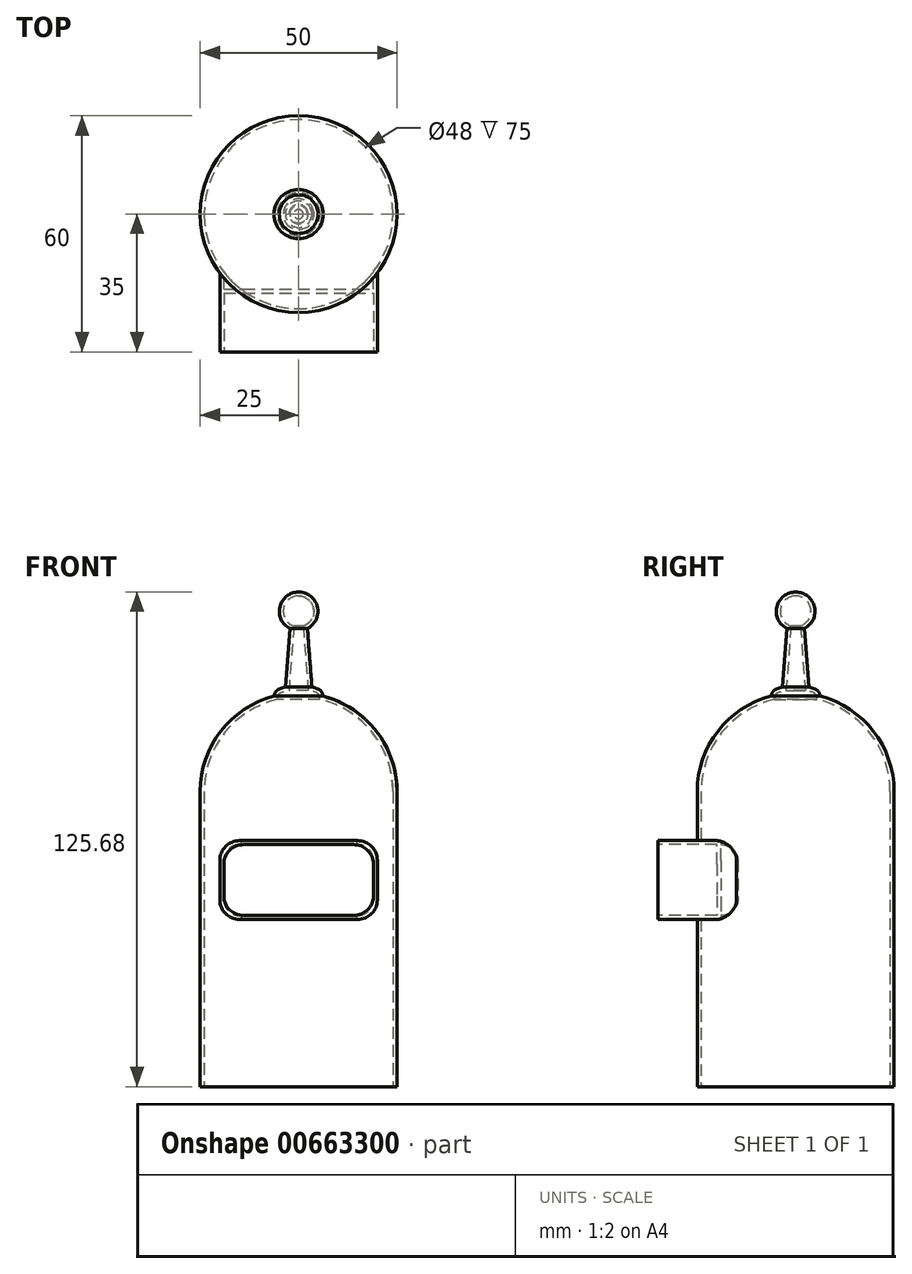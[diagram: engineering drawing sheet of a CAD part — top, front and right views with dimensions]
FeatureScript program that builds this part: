
annotation { "Feature Type Name" : "Feature", "Feature Type Description" : "" }
export const myFeature = defineFeature(function(context is Context, id is Id, definition is map)
    precondition{}
    {
        {
            var Q0;
            Q0=qCreatedBy(makeId("Top.planeOp"),FACE);
            var sketch = newSketch(context, id + "F0", { "sketchPlane" : qUnion([Q0])});
            skCircle(sketch, "E0", {"center": v(0, 0) * mm, "radius": 25 * mm});
            skSolve(sketch);
        }
        {
            var Q0;
            Q0=makeQuery(id+"F0.imprint","IMPRINT",FACE,{"disambiguationData":[TD([[makeQuery(id+"F0.imprint","IMPRINT",EDGE,{"derivedFrom":sQuery(id+"F0.wireOp",EDGE,"E0")}),1.0]])]});
            extrude(context, id + "F1", {"entities" : qUnion([Q0]), "endBound" : BoundingType.SYMMETRIC, "depth" : 75 * mm, "offsetDistance" : 25 * mm});
        }
        {
            var Q0;
            Q0=makeQuery(id+"F1.opExtrude","CAP_EDGE",EDGE,{"disambiguationData":[OSD([sQuery(id+"F0.wireOp",EDGE,"E0")])],"isStart":false});
            fillet(context, id + "F2", {"entities" : qUnion([Q0]), "radius" : 25 * mm, "tangentPropagation" : true, "allowEdgeOverflow" : false});
        }
        {
            var Q0;
            Q0=qCreatedBy(makeId("Front.planeOp"),FACE);
            var sketch = newSketch(context, id + "F3", { "sketchPlane" : qUnion([Q0])});
            skFitSpline(sketch, "E1", {"points": [v(-6.3, 36.49) * mm, v(-5.36, 38.3) * mm, v(-1.59, 39.32) * mm, v(0, 39.5) * mm], "startDerivative": vector(1.54, 6.57) * mm, "endDerivative": vector(4.86, 0.46) * mm});
            skLineSegment(sketch, "E2", {"start": v(-6.3, 36.49) * mm, "end": v(0, 36.49) * mm});
            skLineSegment(sketch, "E3", {"start": v(0, 36.49) * mm, "end": v(0, 39.5) * mm});
            skSolve(sketch);
        }
        {
            var Q0;
            Q0=qCreatedBy(makeId("Front.planeOp"),FACE);
            var sketch = newSketch(context, id + "F4", { "sketchPlane" : qUnion([Q0])});
            skLineSegment(sketch, "E4", {"start": v(0, 58.44) * mm, "end": v(0, 0) * mm, "construction": true});
            skSolve(sketch);
        }
        {
            var Q0;
            Q0=makeQuery(id+"F3.imprint","IMPRINT",FACE,{"disambiguationData":[TD([[makeQuery(id+"F3.imprint","IMPRINT",EDGE,{"derivedFrom":sQuery(id+"F3.wireOp",EDGE,"E1")}),-1.0]])]});
            var Q1;
            Q1=sQuery(id+"F4.wireOp",EDGE,"E4");
            revolve(context, id + "F5", {"operationType" : NewBodyOperationType.ADD, "entities" : qUnion([Q0]), "axis" : qUnion([Q1]), "revolveType" : RevolveType.FULL});
        }
        {
            var Q0;
            Q0=qCreatedBy(makeId("Front.planeOp"),FACE);
            var sketch = newSketch(context, id + "F6", { "sketchPlane" : qUnion([Q0])});
            skLineSegment(sketch, "E5", {"start": v(-3.38, 39.05) * mm, "end": v(-2.1, 55.68) * mm});
            skLineSegment(sketch, "E6", {"start": v(-2.1, 55.68) * mm, "end": v(0, 55.68) * mm});
            skLineSegment(sketch, "E7", {"start": v(0, 55.68) * mm, "end": v(0, 39.05) * mm});
            skLineSegment(sketch, "E8", {"start": v(-3.38, 39.05) * mm, "end": v(-3.38, 38.96) * mm});
            skLineSegment(sketch, "E9", {"start": v(-3.38, 38.96) * mm, "end": v(0, 38.96) * mm});
            skLineSegment(sketch, "E10", {"start": v(0, 38.96) * mm, "end": v(0, 39.05) * mm});
            skSolve(sketch);
        }
        {
            var Q0;
            Q0=makeQuery(id+"F6.imprint","IMPRINT",FACE,{"disambiguationData":[TD([[makeQuery(id+"F6.imprint","IMPRINT",EDGE,{"derivedFrom":sQuery(id+"F6.wireOp",EDGE,"E5")}),-1.0]])]});
            var Q1;
            Q1=sQuery(id+"F6.wireOp",EDGE,"E7");
            revolve(context, id + "F7", {"operationType" : NewBodyOperationType.ADD, "entities" : qUnion([Q0]), "axis" : qUnion([Q1]), "revolveType" : RevolveType.FULL});
        }
        {
            var Q0;
            Q0=qCreatedBy(makeId("Front.planeOp"),FACE);
            var sketch = newSketch(context, id + "F8", { "sketchPlane" : qUnion([Q0])});
            skArc(sketch, "E11", {"start": v(0, 63.18) * mm, "mid": v(-4.9, 58.28) * mm, "end": v(0, 53.38) * mm});
            skLineSegment(sketch, "E12", {"start": v(0, 53.38) * mm, "end": v(0, 63.18) * mm});
            skSolve(sketch);
        }
        {
            var Q0;
            Q0=makeQuery(id+"F8.imprint","IMPRINT",FACE,{"disambiguationData":[TD([[makeQuery(id+"F8.imprint","IMPRINT",EDGE,{"derivedFrom":sQuery(id+"F8.wireOp",EDGE,"E11")}),1.0]])]});
            var Q1;
            Q1=sQuery(id+"F8.wireOp",EDGE,"E12");
            revolve(context, id + "F9", {"operationType" : NewBodyOperationType.ADD, "entities" : qUnion([Q0]), "axis" : qUnion([Q1]), "revolveType" : RevolveType.FULL});
        }
        {
            var Q0;
            Q0=makeQuery(id+"F1.opExtrude","CAP_FACE",FACE,{"disambiguationData":[OSD([sQuery(id+"F0.wireOp",EDGE,"E0")])],"isStart":true});
            extrude(context, id + "F10", {"entities" : qUnion([Q0]), "operationType" : NewBodyOperationType.ADD, "depth" : 25 * mm, "offsetDistance" : 25 * mm});
        }
        {
            var Q0;
            Q0=qCreatedBy(makeId("Front.planeOp"),FACE);
            var sketch = newSketch(context, id + "F11", { "sketchPlane" : qUnion([Q0])});
            skLineSegment(sketch, "E13", {"start": v(0, 0) * mm, "end": v(-15, 0) * mm});
            skLineSegment(sketch, "E14", {"start": v(-20, -5) * mm, "end": v(-20, -15) * mm});
            skLineSegment(sketch, "E15", {"start": v(-15, -20) * mm, "end": v(15, -20) * mm});
            skLineSegment(sketch, "E16", {"start": v(20, -15) * mm, "end": v(20, -5) * mm});
            skLineSegment(sketch, "E17", {"start": v(15, 0) * mm, "end": v(0, 0) * mm});
            skPoint(sketch, "E18.visualSharp", {"position": v(-20, 0) * mm});
            skArc(sketch, "E18.filletArc", {"start": v(-15, 0) * mm, "mid": v(-18.54, -1.46) * mm, "end": v(-20, -5) * mm});
            skPoint(sketch, "E19.visualSharp", {"position": v(-20, -20) * mm});
            skArc(sketch, "E19.filletArc", {"start": v(-20, -15) * mm, "mid": v(-18.54, -18.54) * mm, "end": v(-15, -20) * mm});
            skPoint(sketch, "E20.visualSharp", {"position": v(20, -20) * mm});
            skArc(sketch, "E20.filletArc", {"start": v(15, -20) * mm, "mid": v(18.54, -18.54) * mm, "end": v(20, -15) * mm});
            skPoint(sketch, "E21.visualSharp", {"position": v(20, 0) * mm});
            skArc(sketch, "E21.filletArc", {"start": v(20, -5) * mm, "mid": v(18.54, -1.46) * mm, "end": v(15, 0) * mm});
            skSolve(sketch);
        }
        {
            var Q0;
            Q0 = qSketchRegion(id + "F11", true);
            extrude(context, id + "F12", {"entities" : qUnion([Q0]), "operationType" : NewBodyOperationType.ADD, "depth" : 35 * mm, "offsetDistance" : 25 * mm});
        }
        {
            var Q0;
            Q0=makeQuery(id+"F12.opExtrude","CAP_FACE",FACE,{"disambiguationData":[OSD([sQuery(id+"F11.wireOp",EDGE,"E13"),sQuery(id+"F11.wireOp",EDGE,"E14"),sQuery(id+"F11.wireOp",EDGE,"E15"),sQuery(id+"F11.wireOp",EDGE,"E16"),sQuery(id+"F11.wireOp",EDGE,"E17"),sQuery(id+"F11.wireOp",EDGE,"E18.filletArc"),sQuery(id+"F11.wireOp",EDGE,"E19.filletArc"),sQuery(id+"F11.wireOp",EDGE,"E20.filletArc"),sQuery(id+"F11.wireOp",EDGE,"E21.filletArc")])],"isStart":false});
            var sketch = newSketch(context, id + "F13", { "sketchPlane" : qUnion([Q0])});
            skLineSegment(sketch, "E22", {"start": v(-20, -10) * mm, "end": v(0, -10) * mm, "construction": true});
            skLineSegment(sketch, "E23", {"start": v(0, -10) * mm, "end": v(0, 0) * mm, "construction": true});
            skLineSegment(sketch, "E24.bottom", {"start": v(-14, -1) * mm, "end": v(14, -1) * mm});
            skLineSegment(sketch, "E24.top", {"start": v(-14, -19) * mm, "end": v(14, -19) * mm});
            skLineSegment(sketch, "E24.left", {"start": v(-19, -6) * mm, "end": v(-19, -14) * mm});
            skLineSegment(sketch, "E24.right", {"start": v(19, -6) * mm, "end": v(19, -14) * mm});
            skPoint(sketch, "E24.middle", {"position": v(0, -10) * mm});
            skPoint(sketch, "E25.visualSharp", {"position": v(-19, -1) * mm});
            skArc(sketch, "E25.filletArc", {"start": v(-14, -1) * mm, "mid": v(-17.54, -2.46) * mm, "end": v(-19, -6) * mm});
            skPoint(sketch, "E26.visualSharp", {"position": v(-19, -19) * mm});
            skArc(sketch, "E26.filletArc", {"start": v(-19, -14) * mm, "mid": v(-17.54, -17.54) * mm, "end": v(-14, -19) * mm});
            skPoint(sketch, "E27.visualSharp", {"position": v(19, -19) * mm});
            skArc(sketch, "E27.filletArc", {"start": v(14, -19) * mm, "mid": v(17.54, -17.54) * mm, "end": v(19, -14) * mm});
            skPoint(sketch, "E28.visualSharp", {"position": v(19, -1) * mm});
            skArc(sketch, "E28.filletArc", {"start": v(19, -6) * mm, "mid": v(17.54, -2.46) * mm, "end": v(14, -1) * mm});
            skSolve(sketch);
        }
        {
            var Q0;
            Q0 = qSketchRegion(id + "F13", true);
            var Q1;
            Q1=makeQuery(id+"F13.imprint","IMPRINT",FACE,{"disambiguationData":[TD([[makeQuery(id+"F13.imprint","IMPRINT",EDGE,{"derivedFrom":sQuery(id+"F13.wireOp",EDGE,"E24.bottom")}),-1.0]])]});
            extrude(context, id + "F14", {"entities" : qUnion([Q0, Q1]), "operationType" : NewBodyOperationType.REMOVE, "oppositeDirection" : true, "depth" : 15 * mm, "offsetDistance" : 25 * mm});
        }
        {
            var Q0;
            Q0=makeQuery(id+"F10.opExtrude","CAP_FACE",FACE,{"disambiguationData":[OSD([sQuery(id+"F0.wireOp",EDGE,"E0")])],"isStart":false});
            shell(context, id + "F15", {"entities" : qUnion([Q0]), "thickness" : 1 * mm});
        }
    });
